# Revit family: ВЦН_ЕС
name_source: partatom
category: Mechanical Equipment
units: mm (PartAtom-declared; Revit-internal decimal feet)

## family parameters
Always vertical = Yes
Classification = None
Cut with Voids When Loaded = No
Part Type = Normal
Room Calculation Point = No
Round Connector Dimension = Use Diameter
Shared = No
Work Plane-Based = No

## types (16) — shared parameters
00_20_Виробник = Вентс
00_20_Назва = Витяжний відцентровий вентилятор
Description = Зовнішній настінний монтаж
Manufacturer = Вентс
URL = https://vents.ua
Класифікація навантаження = HVAC
Кількість фаз = 1
Матеріал зони обслуговуваня = <By Category>
Матеріал корпусу = Метал, пофарбований, синій, матовий RAL 5007
Напруга = 230 V
Частота = 50 Hz
zero-valued in all types: Default Elevation

## per-type parameters (varying)
- ВЦН 100: B=260 mm; B1=256 mm  [stored 0.839895 ft]; D=100 mm  [stored 0.328084 ft]; H=355 mm; L=138 mm  [stored 0.452756 ft]; L1=46 mm; L2=92 mm; R=50 mm  [stored 0.164042 ft]; R1=65 mm; R3=52 mm; b1=128 mm; h=178 mm; Вага=3.82 kg; Вертикаль=10; Висота=355 mm; Горизонт=9; Довжина=260 mm; Діаметр=100 mm  [stored 0.328084 ft]; Максимальний потік повітря=325.0 m³/h; Потужність=71 W; Рівень звукового тиску на відстані 3 м=54 дБА; Струм=0 A; Температура повітря, що переміщається=55 °C; Установлена потужність=71 VA; Ширина=138 mm  [stored 0.452756 ft]
- ВЦН 200: B=300 mm; B1=296 mm; D=200 mm  [stored 0.656168 ft]; H=400 mm; L=138 mm  [stored 0.452756 ft]; L1=46 mm; L2=92 mm; R=100 mm  [stored 0.328084 ft]; R1=130 mm  [stored 0.426509 ft]; R3=102 mm; b1=148 mm; h=200 mm  [stored 0.656168 ft]; Вага=4.62 kg; Вертикаль=11; Висота=400 mm; Горизонт=9; Довжина=300 mm; Діаметр=200 mm  [stored 0.656168 ft]; Максимальний потік повітря=700.0 m³/h; Потужність=96 W; Рівень звукового тиску на відстані 3 м=62 дБА; Струм=0 A; Температура повітря, що переміщається=55 °C; Установлена потужність=97 VA; Ширина=138 mm  [stored 0.452756 ft]
- ВЦН 125: B=260 mm; B1=256 mm  [stored 0.839895 ft]; D=125 mm; H=355 mm; L=138 mm  [stored 0.452756 ft]; L1=46 mm; L2=92 mm; R=63 mm; R1=81 mm; R3=64 mm; b1=128 mm; h=178 mm; Вага=3.82 kg; Вертикаль=10; Висота=355 mm; Горизонт=9; Довжина=260 mm; Діаметр=125 mm; Максимальний потік повітря=485.0 m³/h; Потужність=75 W; Рівень звукового тиску на відстані 3 м=54 дБА; Струм=0 A; Температура повітря, що переміщається=55 °C; Установлена потужність=76 VA; Ширина=138 mm  [stored 0.452756 ft]
- ВЦН 150: B=300 mm; B1=296 mm; D=150 mm; H=400 mm; L=138 mm  [stored 0.452756 ft]; L1=46 mm; L2=92 mm; R=75 mm; R1=98 mm  [stored 0.321522 ft]; R3=77 mm  [stored 0.252625 ft]; b1=148 mm; h=200 mm  [stored 0.656168 ft]; Вага=4.53 kg; Вертикаль=11; Висота=400 mm; Горизонт=9; Довжина=300 mm; Діаметр=150 mm; Максимальний потік повітря=630.0 m³/h; Потужність=96 W; Рівень звукового тиску на відстані 3 м=58 дБА; Струм=0 A; Температура повітря, що переміщається=55 °C; Установлена потужність=97 VA; Ширина=138 mm  [stored 0.452756 ft]
- ВЦН 160: B=300 mm; B1=296 mm; D=160 mm  [stored 0.524934 ft]; H=400 mm; L=138 mm  [stored 0.452756 ft]; L1=46 mm; L2=92 mm; R=80 mm  [stored 0.262467 ft]; R1=104 mm  [stored 0.341207 ft]; R3=82 mm; b1=148 mm; h=200 mm  [stored 0.656168 ft]; Вага=4.53 kg; Вертикаль=11; Висота=400 mm; Горизонт=9; Довжина=300 mm; Діаметр=160 mm  [stored 0.524934 ft]; Максимальний потік повітря=650.0 m³/h; Потужність=95 W; Рівень звукового тиску на відстані 3 м=60 дБА; Струм=0 A; Температура повітря, що переміщається=55 °C; Установлена потужність=94 VA; Ширина=138 mm  [stored 0.452756 ft]
- ВЦН 200 К: B=300 mm; B1=296 mm; D=200 mm  [stored 0.656168 ft]; H=400 mm; L=138 mm  [stored 0.452756 ft]; L1=46 mm; L2=92 mm; R=100 mm  [stored 0.328084 ft]; R1=130 mm  [stored 0.426509 ft]; R3=102 mm; b1=148 mm; h=200 mm  [stored 0.656168 ft]; Вага=4.62 kg; Вертикаль=11; Висота=400 mm; Горизонт=9; Довжина=300 mm; Діаметр=200 mm  [stored 0.656168 ft]; Максимальний потік повітря=640.0 m³/h; Потужність=96 W; Рівень звукового тиску на відстані 3 м=62 дБА; Струм=0 A; Температура повітря, що переміщається=55 °C; Установлена потужність=97 VA; Ширина=138 mm  [stored 0.452756 ft]
- ВЦН 160 К: B=300 mm; B1=296 mm; D=160 mm  [stored 0.524934 ft]; H=400 mm; L=138 mm  [stored 0.452756 ft]; L1=46 mm; L2=92 mm; R=80 mm  [stored 0.262467 ft]; R1=104 mm  [stored 0.341207 ft]; R3=82 mm; b1=148 mm; h=200 mm  [stored 0.656168 ft]; Вага=4.53 kg; Вертикаль=11; Висота=400 mm; Горизонт=9; Довжина=300 mm; Діаметр=160 mm  [stored 0.524934 ft]; Максимальний потік повітря=590.0 m³/h; Потужність=95 W; Рівень звукового тиску на відстані 3 м=60 дБА; Струм=0 A; Температура повітря, що переміщається=55 °C; Установлена потужність=94 VA; Ширина=138 mm  [stored 0.452756 ft]
- ВЦН 150 К: B=300 mm; B1=296 mm; D=150 mm; H=400 mm; L=138 mm  [stored 0.452756 ft]; L1=46 mm; L2=92 mm; R=75 mm; R1=98 mm  [stored 0.321522 ft]; R3=77 mm  [stored 0.252625 ft]; b1=148 mm; h=200 mm  [stored 0.656168 ft]; Вага=4.53 kg; Вертикаль=11; Висота=400 mm; Горизонт=9; Довжина=300 mm; Діаметр=150 mm; Максимальний потік повітря=565.0 m³/h; Потужність=96 W; Рівень звукового тиску на відстані 3 м=58 дБА; Струм=0 A; Температура повітря, що переміщається=55 °C; Установлена потужність=97 VA; Ширина=138 mm  [stored 0.452756 ft]
- ВЦН 125 К: B=260 mm; B1=256 mm  [stored 0.839895 ft]; D=125 mm; H=355 mm; L=138 mm  [stored 0.452756 ft]; L1=46 mm; L2=92 mm; R=63 mm; R1=81 mm; R3=64 mm; b1=128 mm; h=178 mm; Вага=3.82 kg; Вертикаль=10; Висота=355 mm; Горизонт=9; Довжина=260 mm; Діаметр=125 mm; Максимальний потік повітря=450.0 m³/h; Потужність=75 W; Рівень звукового тиску на відстані 3 м=54 дБА; Струм=0 A; Температура повітря, що переміщається=55 °C; Установлена потужність=76 VA; Ширина=138 mm  [stored 0.452756 ft]
- ВЦН 100 К: B=260 mm; B1=256 mm  [stored 0.839895 ft]; D=100 mm  [stored 0.328084 ft]; H=355 mm; L=138 mm  [stored 0.452756 ft]; L1=46 mm; L2=92 mm; R=50 mm  [stored 0.164042 ft]; R1=65 mm; R3=52 mm; b1=128 mm; h=178 mm; Вага=3.82 kg; Вертикаль=10; Висота=355 mm; Горизонт=9; Довжина=260 mm; Діаметр=100 mm  [stored 0.328084 ft]; Максимальний потік повітря=295.0 m³/h; Потужність=71 W; Рівень звукового тиску на відстані 3 м=54 дБА; Струм=0 A; Температура повітря, що переміщається=55 °C; Установлена потужність=71 VA; Ширина=138 mm  [stored 0.452756 ft]
- ВЦН 100 EC: B=260 mm; B1=256 mm  [stored 0.839895 ft]; D=100 mm  [stored 0.328084 ft]; H=355 mm; L=140 mm  [stored 0.459318 ft]; L1=47 mm; L2=93 mm; R=50 mm  [stored 0.164042 ft]; R1=65 mm; R3=52 mm; b1=128 mm; h=178 mm; Вага=3.60 kg; Вертикаль=10; Висота=355 mm; Горизонт=9; Довжина=260 mm; Діаметр=100 mm  [stored 0.328084 ft]; Максимальний потік повітря=313.0 m³/h; Потужність=89 W; Рівень звукового тиску на відстані 3 м=55 дБА; Струм=1 A; Температура повітря, що переміщається=-25...+40 °C; Установлена потужність=122 VA; Ширина=140 mm  [stored 0.459318 ft]
- ВЦН 125 ЕС: B=260 mm; B1=256 mm  [stored 0.839895 ft]; D=125 mm; H=355 mm; L=140 mm  [stored 0.459318 ft]; L1=47 mm; L2=93 mm; R=63 mm; R1=81 mm; R3=64 mm; b1=128 mm; h=178 mm; Вага=3.60 kg; Вертикаль=10; Висота=355 mm; Горизонт=9; Довжина=260 mm; Діаметр=125 mm; Максимальний потік повітря=480.0 m³/h; Потужність=103 W; Рівень звукового тиску на відстані 3 м=57 дБА; Струм=1 A; Температура повітря, що переміщається=-25...+40 °C; Установлена потужність=191 VA; Ширина=140 mm  [stored 0.459318 ft]
- ВЦН 150 ЕС: B=300 mm; B1=296 mm; D=150 mm; H=400 mm; L=140 mm  [stored 0.459318 ft]; L1=47 mm; L2=93 mm; R=75 mm; R1=98 mm  [stored 0.321522 ft]; R3=77 mm  [stored 0.252625 ft]; b1=148 mm; h=200 mm  [stored 0.656168 ft]; Вага=4.70 kg; Вертикаль=11; Висота=400 mm; Горизонт=9; Довжина=300 mm; Діаметр=150 mm; Максимальний потік повітря=550.0 m³/h; Потужність=92 W; Рівень звукового тиску на відстані 3 м=56 дБА; Струм=1 A; Температура повітря, що переміщається=-25...+40 °C; Установлена потужність=173 VA; Ширина=140 mm  [stored 0.459318 ft]
- ВЦН 160 ЕС: B=300 mm; B1=296 mm; D=160 mm  [stored 0.524934 ft]; H=400 mm; L=140 mm  [stored 0.459318 ft]; L1=47 mm; L2=93 mm; R=80 mm  [stored 0.262467 ft]; R1=104 mm  [stored 0.341207 ft]; R3=82 mm; b1=148 mm; h=200 mm  [stored 0.656168 ft]; Вага=4.70 kg; Вертикаль=11; Висота=400 mm; Горизонт=9; Довжина=300 mm; Діаметр=160 mm  [stored 0.524934 ft]; Максимальний потік повітря=585.0 m³/h; Потужність=92 W; Рівень звукового тиску на відстані 3 м=55 дБА; Струм=1 A; Температура повітря, що переміщається=-25...+40 °C; Установлена потужність=173 VA; Ширина=140 mm  [stored 0.459318 ft]
- ВЦН 200 ЕС: B=300 mm; B1=296 mm; D=200 mm  [stored 0.656168 ft]; H=400 mm; L=140 mm  [stored 0.459318 ft]; L1=47 mm; L2=93 mm; R=100 mm  [stored 0.328084 ft]; R1=130 mm  [stored 0.426509 ft]; R3=102 mm; b1=148 mm; h=200 mm  [stored 0.656168 ft]; Вага=4.70 kg; Вертикаль=11; Висота=400 mm; Горизонт=9; Довжина=300 mm; Діаметр=200 mm  [stored 0.656168 ft]; Максимальний потік повітря=535.0 m³/h; Потужність=79 W; Рівень звукового тиску на відстані 3 м=55 дБА; Струм=1 A; Температура повітря, що переміщається=-25...+40 °C; Установлена потужність=154 VA; Ширина=140 mm  [stored 0.459318 ft]
- ВЦН 200 ЕС С: B=325 mm  [stored 1.06627 ft]; B1=321 mm  [stored 1.05315 ft]; D=200 mm  [stored 0.656168 ft]; H=400 mm; L=181 mm; L1=60 mm  [stored 0.19685 ft]; L2=121 mm  [stored 0.396982 ft]; R=100 mm  [stored 0.328084 ft]; R1=130 mm  [stored 0.426509 ft]; R3=102 mm; b1=161 mm; h=200 mm  [stored 0.656168 ft]; Вага=5.30 kg; Вертикаль=12; Висота=400 mm; Горизонт=8; Довжина=325 mm  [stored 1.06627 ft]; Діаметр=200 mm  [stored 0.656168 ft]; Максимальний потік повітря=755.0 m³/h; Потужність=102 W; Рівень звукового тиску на відстані 3 м=58 дБА; Струм=1 A; Температура повітря, що переміщається=-25...+40 °C; Установлена потужність=198 VA; Ширина=181 mm

note: column(s) folded — value = type name in every type: 00_20_Тип

note: [stored X ft] marks values corroborated as IEEE doubles in the binary element streams (Revit-internal decimal feet)
